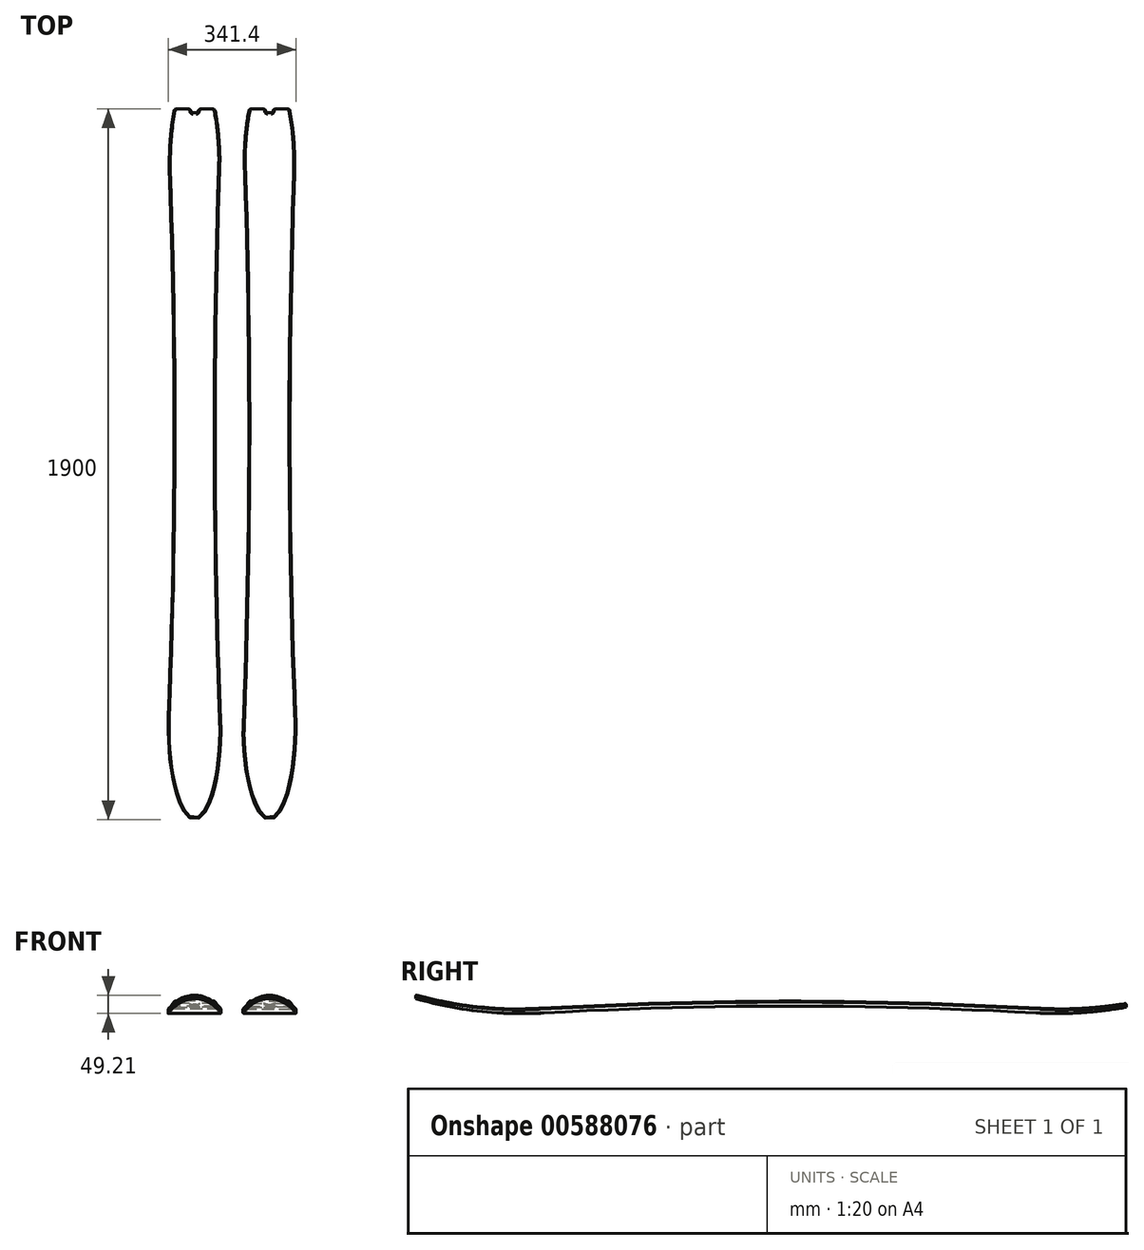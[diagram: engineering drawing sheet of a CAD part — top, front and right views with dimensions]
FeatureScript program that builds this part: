
annotation { "Feature Type Name" : "Feature", "Feature Type Description" : "" }
export const myFeature = defineFeature(function(context is Context, id is Id, definition is map)
    precondition{}
    {
        {
            var Q0;
            Q0=qCreatedBy(makeId("Top.planeOp"),FACE);
            var sketch = newSketch(context, id + "F0", { "sketchPlane" : qUnion([Q0])});
            skLineSegment(sketch, "E0", {"start": v(-55, 0) * mm, "end": v(55, 0) * mm, "construction": true});
            skPoint(sketch, "E1", {"position": v(0, 0) * mm});
            skLineSegment(sketch, "E2", {"start": v(55, 0) * mm, "end": v(19055, 0) * mm, "construction": true});
            skLineSegment(sketch, "E3", {"start": v(-55, 0) * mm, "end": v(-21055, 0) * mm, "construction": true});
            skLineSegment(sketch, "E4.0", {"start": v(-171.97, -90) * mm, "end": v(164.88, -90) * mm, "construction": true});
            skPoint(sketch, "E5", {"position": v(-3.54, -90) * mm});
            skLineSegment(sketch, "E6.0", {"start": v(-150, -1040) * mm, "end": v(83.48, -1040) * mm, "construction": true});
            skLineSegment(sketch, "E7.0", {"start": v(-54.13, 860) * mm, "end": v(-10, 860) * mm});
            skArc(sketch, "E8", {"start": v(67.08, 677.33) * mm, "mid": v(55.04, -38.95) * mm, "end": v(70.01, -755.18) * mm});
            skArc(sketch, "E9", {"start": v(-67.53, 725.32) * mm, "mid": v(-55.04, -41.1) * mm, "end": v(-70.53, -807.48) * mm});
            skEllipticalArc(sketch, "E10", {});
            skEllipticalArc(sketch, "E11", {});
            skLineSegment(sketch, "E12.0", {"start": v(-72.62, 960) * mm, "end": v(74.47, 960) * mm, "construction": true});
            skEllipticalArc(sketch, "E13.trimOffspring", {});
            skLineSegment(sketch, "E14.top", {"start": v(10, 850) * mm, "end": v(-10, 850) * mm});
            skLineSegment(sketch, "E14.left", {"start": v(10, 860) * mm, "end": v(10, 850) * mm});
            skLineSegment(sketch, "E14.right", {"start": v(-10, 860) * mm, "end": v(-10, 850) * mm});
            skPoint(sketch, "E14.middle", {"position": v(0, 860) * mm});
            skLineSegment(sketch, "E15.trimOffspring", {"start": v(10, 860) * mm, "end": v(54.13, 860) * mm});
            skPoint(sketch, "E14.bottom.start.orphan", {"position": v(10, 870) * mm});
            skPoint(sketch, "E16.orphan", {"position": v(-10, 870) * mm});
            skLineSegment(sketch, "E17", {"start": v(-150, -1040) * mm, "end": v(-150, 860) * mm, "construction": true});
            skLineSegment(sketch, "E18", {"start": v(-54.13, 860) * mm, "end": v(-150, 860) * mm, "construction": true});
            skEllipticalArc(sketch, "E19.MirrorCS", {});
            skLineSegment(sketch, "E20.MirrorCS", {"start": v(-245.87, 860) * mm, "end": v(-290, 860) * mm});
            skLineSegment(sketch, "E21.MirrorCS", {"start": v(-290, 860) * mm, "end": v(-290, 850) * mm});
            skLineSegment(sketch, "E22.MirrorCS", {"start": v(-310, 850) * mm, "end": v(-290, 850) * mm});
            skLineSegment(sketch, "E23.MirrorCS", {"start": v(-310, 860) * mm, "end": v(-310, 850) * mm});
            skLineSegment(sketch, "E24.MirrorCS", {"start": v(-310, 860) * mm, "end": v(-354.13, 860) * mm});
            skEllipticalArc(sketch, "E25.MirrorCS", {});
            skArc(sketch, "E26.MirrorCS", {"start": v(-232.47, 725.32) * mm, "mid": v(-244.96, -41.1) * mm, "end": v(-229.47, -807.48) * mm});
            skArc(sketch, "E27.MirrorCS", {"start": v(-367.08, 677.33) * mm, "mid": v(-355.04, -38.95) * mm, "end": v(-370.01, -755.18) * mm});
            skEllipticalArc(sketch, "E28.MirrorCS", {});
            const initialGuessF0  = {"E10": [0, -0.79, 0, -1, 0.25, 0.07070288150256428, 4.782346897338015, 1.7105307733128072], "E11": [0, 0.71, 1, 0, 0.06765707543196828, 0.25, 2.498091544796518, 3.0802544398139586], "E13.trimOffspring": [0, 0.71, 1, 0, 0.06765707543196828, 0.25, 6.152130419772989, 0.6435011087932754], "E19.MirrorCS": [-0.3, 0.71, -1, 0, 0.06765707543196828, 0.25, 3.2029308673656276, 3.785093762383068], "E25.MirrorCS": [-0.3, 0.71, -1, 0, 0.06765707543196828, 0.25, 5.639684198386311, 0.13105488740659688], "E28.MirrorCS": [-0.3, -0.79, 0, -1, 0.25, 0.07070288150256428, 4.572654533866779, 1.5008384098415712]};
            skSetInitialGuess(sketch, initialGuessF0);
            skSolve(sketch);
        }
        {
            var Q0;
            Q0 = qSketchRegion(id + "F0", true);
            extrude(context, id + "F1", {"entities" : qUnion([Q0]), "depth" : 200 * mm, "offsetDistance" : 25 * mm});
        }
        {
            var Q0;
            Q0=qCreatedBy(makeId("Right.planeOp"),FACE);
            var sketch = newSketch(context, id + "F2", { "sketchPlane" : qUnion([Q0])});
            skLineSegment(sketch, "E29.bottom", {"start": v(860, -150) * mm, "end": v(-1040, -150) * mm});
            skLineSegment(sketch, "E29.top", {"start": v(860, 350) * mm, "end": v(-1040, 350) * mm});
            skLineSegment(sketch, "E29.left", {"start": v(860, -150) * mm, "end": v(860, 17.08) * mm});
            skLineSegment(sketch, "E29.right", {"start": v(-1040, -150) * mm, "end": v(-1040, 40) * mm});
            skPoint(sketch, "E29.middle", {"position": v(-90, 100) * mm});
            skArc(sketch, "E30", {"start": v(-1040, 40) * mm, "mid": v(-870.21, 6.43) * mm, "end": v(-697.2, 1.61) * mm});
            skPoint(sketch, "E30.first.point", {"position": v(-755, 0) * mm});
            skPoint(sketch, "E30.third.point", {"position": v(21.03, 350) * mm});
            skArc(sketch, "E31", {"start": v(619.2, 1.61) * mm, "mid": v(-39, 20) * mm, "end": v(-697.2, 1.61) * mm});
            skArc(sketch, "E32.trimOffspring", {"start": v(619.2, 1.61) * mm, "mid": v(740.06, 2.3) * mm, "end": v(860, 17.08) * mm});
            skPoint(sketch, "E33.center.orphan", {"position": v(677, 1035.31) * mm});
            skPoint(sketch, "E34", {"position": v(860, 27.08) * mm});
            skArc(sketch, "E35", {"start": v(629.1, 13.98) * mm, "mid": v(-39, 32.9) * mm, "end": v(-707.1, 13.98) * mm});
            skArc(sketch, "E36", {"start": v(-1040, 50) * mm, "mid": v(-875.03, 18.28) * mm, "end": v(-707.1, 13.98) * mm});
            skArc(sketch, "E37", {"start": v(629.1, 13.98) * mm, "mid": v(744.92, 13.98) * mm, "end": v(860, 27.08) * mm});
            skLineSegment(sketch, "E38.trimOffspring", {"start": v(-1040, 50) * mm, "end": v(-1040, 350) * mm});
            skPoint(sketch, "E39.orphan", {"position": v(-1040, 100) * mm});
            skPoint(sketch, "E40.end.orphan", {"position": v(860, 100) * mm});
            skLineSegment(sketch, "E41.trimOffspring", {"start": v(860, 27.08) * mm, "end": v(860, 350) * mm});
            skSolve(sketch);
        }
        {
            var Q0;
            Q0 = qSketchRegion(id + "F2", true);
            extrude(context, id + "F3", {"entities" : qUnion([Q0]), "operationType" : NewBodyOperationType.REMOVE, "endBound" : BoundingType.THROUGH_ALL, "oppositeDirection" : true, "depth" : 25 * mm, "offsetDistance" : 25 * mm});
        }
        {
            var Q0;
            Q0 = qSketchRegion(id + "F2", true);
            extrude(context, id + "F4", {"entities" : qUnion([Q0]), "operationType" : NewBodyOperationType.REMOVE, "endBound" : BoundingType.THROUGH_ALL, "depth" : 25 * mm, "offsetDistance" : 25 * mm});
        }
        {
            var Q0;
            Q0=makeQuery(id+"F1.opExtrude","SWEPT_EDGE",EDGE,{"disambiguationData":[OSD([sQuery(id+"F0.wireOp",EDGE,"E13.trimOffspring"),sQuery(id+"F0.wireOp",EDGE,"E15.trimOffspring")])]});
            var Q1;
            Q1=makeQuery(id+"F1.opExtrude","SWEPT_EDGE",EDGE,{"disambiguationData":[OSD([sQuery(id+"F0.wireOp",EDGE,"E14.left"),sQuery(id+"F0.wireOp",EDGE,"E15.trimOffspring")])]});
            var Q2;
            Q2=makeQuery(id+"F1.opExtrude","SWEPT_EDGE",EDGE,{"disambiguationData":[OSD([sQuery(id+"F0.wireOp",EDGE,"E14.top"),sQuery(id+"F0.wireOp",EDGE,"E14.left")])]});
            var Q3;
            Q3=makeQuery(id+"F1.opExtrude","SWEPT_EDGE",EDGE,{"disambiguationData":[OSD([sQuery(id+"F0.wireOp",EDGE,"E7.0"),sQuery(id+"F0.wireOp",EDGE,"E14.right")])]});
            var Q4;
            Q4=makeQuery(id+"F1.opExtrude","SWEPT_EDGE",EDGE,{"disambiguationData":[OSD([sQuery(id+"F0.wireOp",EDGE,"E7.0"),sQuery(id+"F0.wireOp",EDGE,"E11")])]});
            var Q5;
            Q5=makeQuery(id+"F1.opExtrude","SWEPT_EDGE",EDGE,{"disambiguationData":[OSD([sQuery(id+"F0.wireOp",EDGE,"E14.top"),sQuery(id+"F0.wireOp",EDGE,"E14.right")])]});
            fillet(context, id + "F5", {"entities" : qUnion([Q0, Q1, Q2, Q3, Q4, Q5]), "radius" : 5 * mm, "tangentPropagation" : true, "allowEdgeOverflow" : false});
        }
        {
            var Q0;
            {var subQ0=sQuery(id+"F2.wireOp",EDGE,"E36");Q0=makeQuery(id+"F4.boolean.opBoolean","MERGE",FACE,{"derivedFrom":[makeQuery(id+"F3.boolean.opBoolean","COPY",FACE,{"derivedFrom":makeQuery(id+"F3.opExtrude","SWEPT_FACE",FACE,{"disambiguationData":[OSD([subQ0])]})}),makeQuery(id+"F4.opExtrude","SWEPT_FACE",FACE,{"disambiguationData":[OSD([subQ0])]})]});}
            var Q1;
            {var subQ0=sQuery(id+"F2.wireOp",EDGE,"E35");Q1=makeQuery(id+"F4.boolean.opBoolean","MERGE",FACE,{"derivedFrom":[makeQuery(id+"F3.boolean.opBoolean","COPY",FACE,{"derivedFrom":makeQuery(id+"F3.opExtrude","SWEPT_FACE",FACE,{"disambiguationData":[OSD([subQ0])]})}),makeQuery(id+"F4.opExtrude","SWEPT_FACE",FACE,{"disambiguationData":[OSD([subQ0])]})]});}
            var Q2;
            {var subQ0=sQuery(id+"F2.wireOp",EDGE,"E37");Q2=makeQuery(id+"F4.boolean.opBoolean","MERGE",FACE,{"derivedFrom":[makeQuery(id+"F3.boolean.opBoolean","COPY",FACE,{"derivedFrom":makeQuery(id+"F3.opExtrude","SWEPT_FACE",FACE,{"disambiguationData":[OSD([subQ0])]})}),makeQuery(id+"F4.opExtrude","SWEPT_FACE",FACE,{"disambiguationData":[OSD([subQ0])]})]});}
            fillet(context, id + "F6", {"entities" : qUnion([Q0, Q1, Q2]), "radius" : 2.5 * mm, "tangentPropagation" : true, "allowEdgeOverflow" : false});
        }
        {
            var Q0;
            Q0=makeQuery(id+"F1.opExtrude","SWEPT_BODY",BODY,{"disambiguationData":[OSD([sQuery(id+"F0.wireOp",EDGE,"E19.MirrorCS"),sQuery(id+"F0.wireOp",EDGE,"E20.MirrorCS"),sQuery(id+"F0.wireOp",EDGE,"E21.MirrorCS"),sQuery(id+"F0.wireOp",EDGE,"E22.MirrorCS"),sQuery(id+"F0.wireOp",EDGE,"E23.MirrorCS"),sQuery(id+"F0.wireOp",EDGE,"E24.MirrorCS"),sQuery(id+"F0.wireOp",EDGE,"E25.MirrorCS"),sQuery(id+"F0.wireOp",EDGE,"E26.MirrorCS"),sQuery(id+"F0.wireOp",EDGE,"E27.MirrorCS"),sQuery(id+"F0.wireOp",EDGE,"E28.MirrorCS")])]});
            deleteBodies(context, id + "F7", {"entities" : qUnion([Q0])});
        }
        {
            var Q0;
            Q0=qCreatedBy(makeId("Right.planeOp"),FACE);
            cPlane(context, id + "F8", {"entities" : qUnion([Q0]), "cplaneType" : CPlaneType.OFFSET, "offset" : 100 * mm, "oppositeDirection" : true, "width" : 150 * mm, "height" : 150 * mm});
        }
        {
            var Q0;
            Q0=makeQuery(id+"F1.opExtrude","SWEPT_BODY",BODY,{"disambiguationData":[OSD([sQuery(id+"F0.wireOp",EDGE,"E7.0"),sQuery(id+"F0.wireOp",EDGE,"E8"),sQuery(id+"F0.wireOp",EDGE,"E9"),sQuery(id+"F0.wireOp",EDGE,"E10"),sQuery(id+"F0.wireOp",EDGE,"E11"),sQuery(id+"F0.wireOp",EDGE,"E13.trimOffspring"),sQuery(id+"F0.wireOp",EDGE,"E14.top"),sQuery(id+"F0.wireOp",EDGE,"E14.left"),sQuery(id+"F0.wireOp",EDGE,"E14.right"),sQuery(id+"F0.wireOp",EDGE,"E15.trimOffspring")])]});
            var Q1;
            Q1=qCreatedBy(id+"F8.planeOp",FACE);
            mirror(context, id + "F9", {"entities" : qUnion([Q0]), "mirrorPlane" : qUnion([Q1])});
        }
    });
